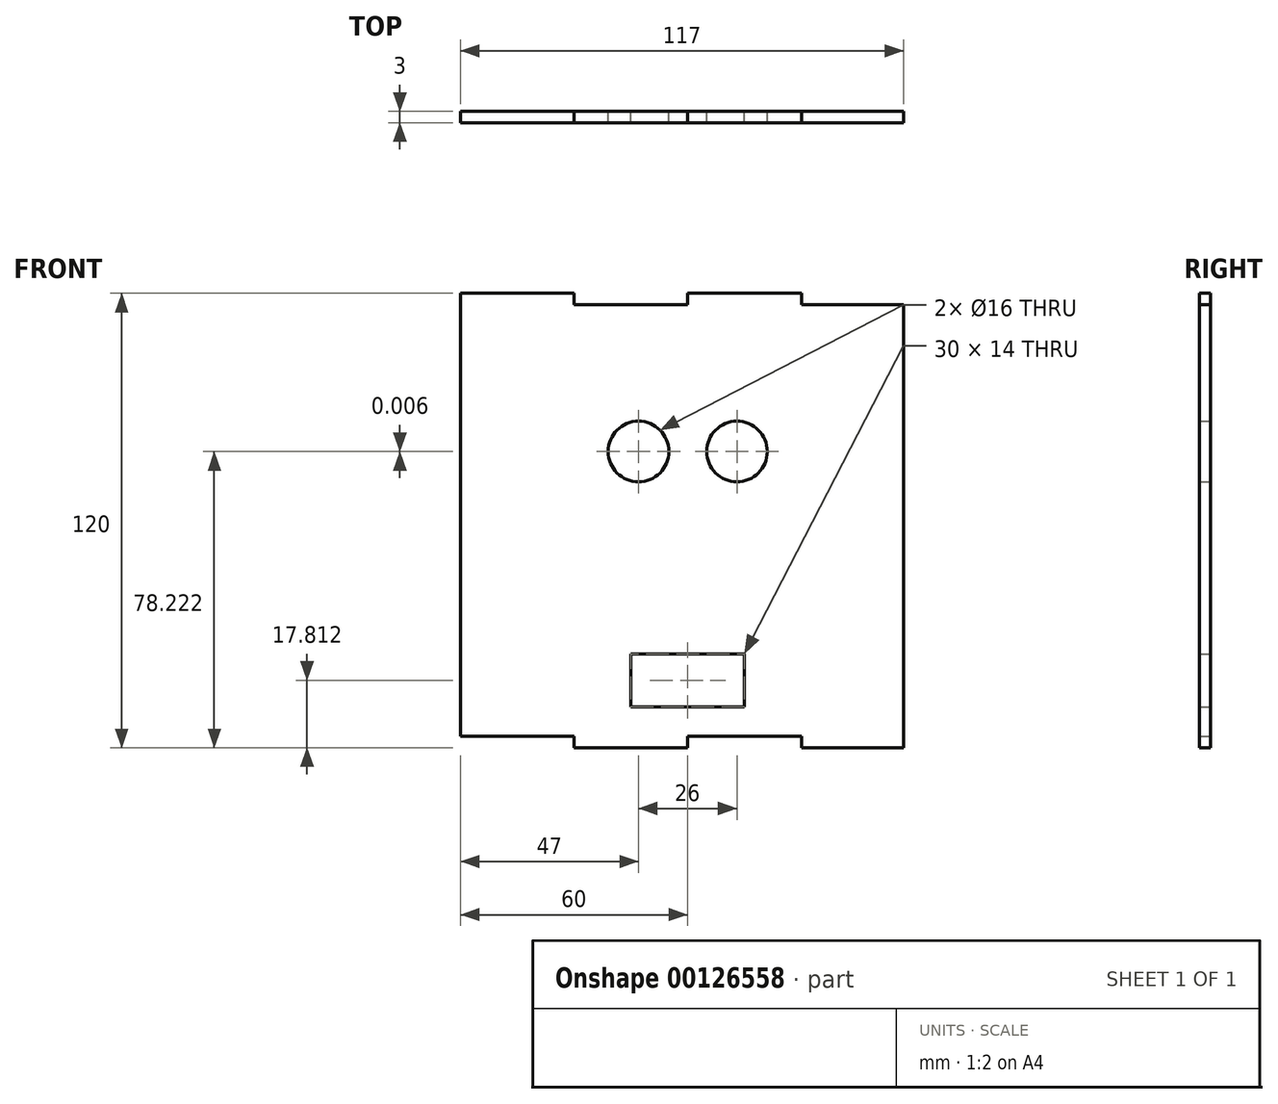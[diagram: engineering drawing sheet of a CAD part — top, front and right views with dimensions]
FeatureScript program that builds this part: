
annotation { "Feature Type Name" : "Feature", "Feature Type Description" : "" }
export const myFeature = defineFeature(function(context is Context, id is Id, definition is map)
    precondition{}
    {
        {
            var Q0;
            Q0=qCreatedBy(makeId("Front.planeOp"),FACE);
            var sketch = newSketch(context, id + "F0", { "sketchPlane" : qUnion([Q0])});
            skLineSegment(sketch, "E0", {"start": v(0, 0) * mm, "end": v(0, 0) * mm});
            skPoint(sketch, "E1.middle", {"position": v(0, 14.81) * mm});
            skPoint(sketch, "E2.middle", {"position": v(0, 75.23) * mm});
            skCircle(sketch, "E3", {"center": v(-13, 75.23) * mm, "radius": 8 * mm});
            skCircle(sketch, "E4.MirrorC", {"center": v(13, 75.22) * mm, "radius": 8 * mm});
            skLineSegment(sketch, "E5", {"start": v(0, 75.23) * mm, "end": v(0, 0) * mm, "construction": true});
            skLineSegment(sketch, "E6", {"start": v(-21, 74.98) * mm, "end": v(21, 75.22) * mm, "construction": true});
            skLineSegment(sketch, "E7", {"start": v(-5, 75.07) * mm, "end": v(5, 75.13) * mm, "construction": true});
            skLineSegment(sketch, "E8", {"start": v(0, 75.23) * mm, "end": v(0, 100) * mm, "construction": true});
            skLineSegment(sketch, "E9", {"start": v(0, 100) * mm, "end": v(0, -3) * mm, "construction": true});
            skLineSegment(sketch, "E10", {"start": v(0, -3) * mm, "end": v(-30, -3) * mm});
            skLineSegment(sketch, "E11", {"start": v(30, -3) * mm, "end": v(57, -3) * mm});
            skLineSegment(sketch, "E12", {"start": v(-60, 0) * mm, "end": v(-30, 0) * mm});
            skLineSegment(sketch, "E13", {"start": v(-30, 0) * mm, "end": v(-30, -3) * mm});
            skLineSegment(sketch, "E14", {"start": v(-30, -3) * mm, "end": v(0, -3) * mm});
            skLineSegment(sketch, "E15", {"start": v(0, -3) * mm, "end": v(0, 0) * mm});
            skLineSegment(sketch, "E16", {"start": v(0, 0) * mm, "end": v(30, 0) * mm});
            skLineSegment(sketch, "E17", {"start": v(30, 0) * mm, "end": v(30, -3) * mm});
            skLineSegment(sketch, "E18", {"start": v(57, -3) * mm, "end": v(57, 114) * mm});
            skLineSegment(sketch, "E19", {"start": v(30, 117) * mm, "end": v(0, 117) * mm});
            skLineSegment(sketch, "E20", {"start": v(-60, 117) * mm, "end": v(-60, 0) * mm});
            skLineSegment(sketch, "E21", {"start": v(-60, 117) * mm, "end": v(-30, 117) * mm});
            skLineSegment(sketch, "E22", {"start": v(-30, 117) * mm, "end": v(-30, 114) * mm});
            skLineSegment(sketch, "E23", {"start": v(-30, 114) * mm, "end": v(0, 114) * mm});
            skLineSegment(sketch, "E24", {"start": v(0, 114) * mm, "end": v(0, 117) * mm});
            skLineSegment(sketch, "E25", {"start": v(0, 117) * mm, "end": v(30, 117) * mm});
            skLineSegment(sketch, "E26", {"start": v(30, 117) * mm, "end": v(30, 114) * mm});
            skLineSegment(sketch, "E27", {"start": v(30, 114) * mm, "end": v(57, 114) * mm});
            skLineSegment(sketch, "E28.trimOffspring", {"start": v(-30, 117) * mm, "end": v(-60, 117) * mm});
            skLineSegment(sketch, "E29.bottom", {"start": v(15, 21.81) * mm, "end": v(-15, 21.81) * mm});
            skLineSegment(sketch, "E29.top", {"start": v(15, 7.81) * mm, "end": v(-15, 7.81) * mm});
            skLineSegment(sketch, "E29.left", {"start": v(15, 21.81) * mm, "end": v(15, 7.81) * mm});
            skLineSegment(sketch, "E29.right", {"start": v(-15, 21.81) * mm, "end": v(-15, 7.81) * mm});
            skSolve(sketch);
        }
        {
            var Q0;
            Q0=makeQuery(id+"F0.imprint","IMPRINT",FACE,{"disambiguationData":[TD([[makeQuery(id+"F0.imprint","IMPRINT",EDGE,{"derivedFrom":sQuery(id+"F0.wireOp",EDGE,"E1.bottom")}),1.0]])]});
            var Q1;
            Q1=makeQuery(id+"F0.imprint","IMPRINT",FACE,{"disambiguationData":[TD([[makeQuery(id+"F0.imprint","IMPRINT",EDGE,{"derivedFrom":sQuery(id+"F0.wireOp",EDGE,"E3")}),-1.0]])]});
            extrude(context, id + "F1", {"entities" : qUnion([Q0, Q1]), "endBound" : BoundingType.SYMMETRIC, "depth" : 3 * mm});
        }
    });
